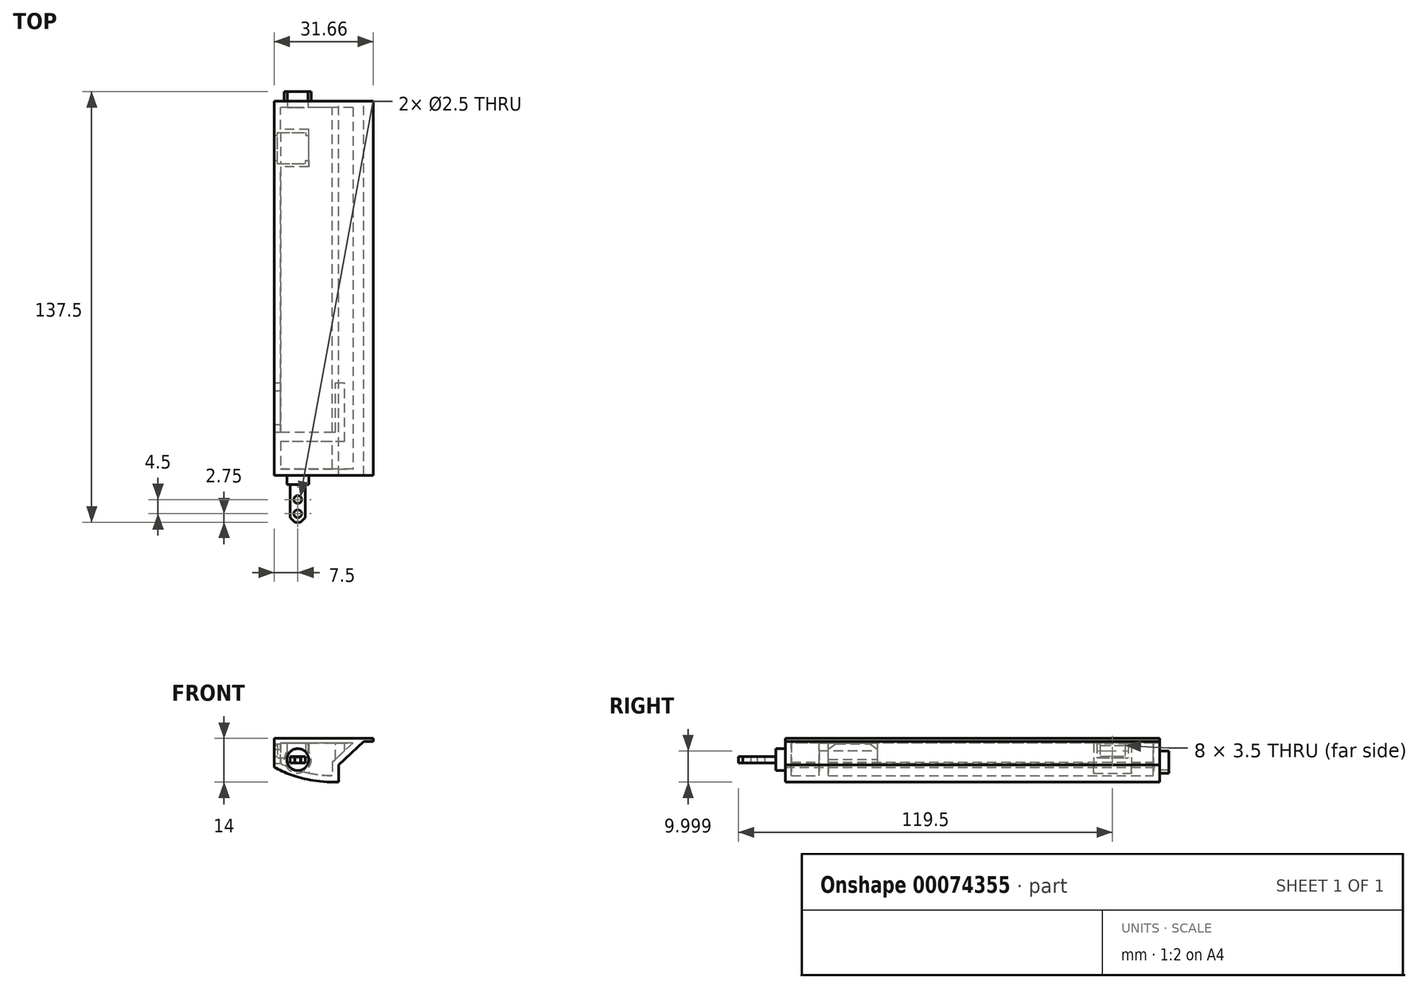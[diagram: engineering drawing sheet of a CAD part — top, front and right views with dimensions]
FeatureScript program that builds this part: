
annotation { "Feature Type Name" : "Feature", "Feature Type Description" : "" }
export const myFeature = defineFeature(function(context is Context, id is Id, definition is map)
    precondition{}
    {
        {
            var Q0;
            Q0=qCreatedBy(makeId("Front.planeOp"),FACE);
            var sketch = newSketch(context, id + "F0", { "sketchPlane" : qUnion([Q0])});
            skCircle(sketch, "E0", {"center": v(7.5, 7.2) * mm, "radius": 4.3 * mm, "construction": true});
            skLineSegment(sketch, "E1", {"start": v(0, 14) * mm, "end": v(31.66, 14) * mm});
            skLineSegment(sketch, "E2", {"start": v(31.66, 13) * mm, "end": v(28.56, 13) * mm});
            skLineSegment(sketch, "E3", {"start": v(28.56, 13) * mm, "end": v(20.5, 5.5) * mm});
            skLineSegment(sketch, "E4", {"start": v(20.5, 5.5) * mm, "end": v(20.5, 0) * mm});
            skFitSpline(sketch, "E5", {"points": [v(20.5, 0) * mm, v(0, 4.8) * mm], "startDerivative": vector(-29.77, 0) * mm, "endDerivative": vector(-14.06, 7.78) * mm});
            skLineSegment(sketch, "E6", {"start": v(0, 10.8) * mm, "end": v(0, 4.8) * mm});
            skLineSegment(sketch, "E7", {"start": v(31.66, 13) * mm, "end": v(31.66, 14) * mm});
            skLineSegment(sketch, "E8", {"start": v(0, 10.8) * mm, "end": v(0, 14) * mm});
            skSolve(sketch);
        }
        {
            var Q0;
            Q0=makeQuery(id+"F0.imprint","IMPRINT",FACE,{"disambiguationData":[TD([[makeQuery(id+"F0.imprint","IMPRINT",EDGE,{"derivedFrom":sQuery(id+"F0.wireOp",EDGE,"E1")}),-1.0]])]});
            extrude(context, id + "F1", {"entities" : qUnion([Q0]), "depth" : 119.5 * mm});
        }
        {
            var Q0;
            Q0=makeQuery(id+"F1.opExtrude","SWEPT_FACE",FACE,{"disambiguationData":[OSD([sQuery(id+"F0.wireOp",EDGE,"E1")])]});
            var Q1;
            Q1=makeQuery(id+"F1.opExtrude","SWEPT_BODY",BODY,{"disambiguationData":[OSD([sQuery(id+"F0.wireOp",EDGE,"E1"),sQuery(id+"F0.wireOp",EDGE,"E2"),sQuery(id+"F0.wireOp",EDGE,"E3"),sQuery(id+"F0.wireOp",EDGE,"E4"),sQuery(id+"F0.wireOp",EDGE,"E5"),sQuery(id+"F0.wireOp",EDGE,"ef3ae709-1856-4767-82a3-158976314dcd"),sQuery(id+"F0.wireOp",EDGE,"E6"),sQuery(id+"F0.wireOp",EDGE,"E7")])]});
            shell(context, id + "F2", {"entities" : qUnion([Q0]), "parts" : qUnion([Q1]), "thickness" : 2 * mm});
        }
        {
            var Q0;
            {var subQ0=sQuery(id+"F0.wireOp",EDGE,"E8");var subQ1=sQuery(id+"F0.wireOp",EDGE,"E7");var subQ2=sQuery(id+"F0.wireOp",EDGE,"E6");var subQ3=sQuery(id+"F0.wireOp",EDGE,"E5");var subQ4=sQuery(id+"F0.wireOp",EDGE,"E4");var subQ5=sQuery(id+"F0.wireOp",EDGE,"E3");var subQ6=sQuery(id+"F0.wireOp",EDGE,"E2");var subQ7=sQuery(id+"F0.wireOp",EDGE,"E1");Q0=makeQuery(id+"F2.opShell","OFFSET_FACE",FACE,{"disambiguationData":[OSD([subQ7,subQ6,subQ5,subQ4,subQ3,subQ2,subQ1,subQ0]),TDD([makeQuery(id+"F1.opExtrude","CAP_FACE",FACE,{"disambiguationData":[OSD([subQ7,subQ6,subQ5,subQ4,subQ3,subQ2,subQ1,subQ0])],"isStart":false})])]});}
            var Q1;
            {var subQ0=sQuery(id+"F0.wireOp",EDGE,"E8");var subQ1=sQuery(id+"F0.wireOp",EDGE,"E7");var subQ2=sQuery(id+"F0.wireOp",EDGE,"E6");var subQ3=sQuery(id+"F0.wireOp",EDGE,"E5");var subQ4=sQuery(id+"F0.wireOp",EDGE,"E4");var subQ5=sQuery(id+"F0.wireOp",EDGE,"E3");var subQ6=sQuery(id+"F0.wireOp",EDGE,"E2");var subQ7=sQuery(id+"F0.wireOp",EDGE,"E1");Q1=makeQuery(id+"F2.opShell","OFFSET_FACE",FACE,{"disambiguationData":[OSD([subQ7,subQ6,subQ5,subQ4,subQ3,subQ2,subQ1,subQ0]),TDD([makeQuery(id+"F1.opExtrude","CAP_FACE",FACE,{"disambiguationData":[OSD([subQ7,subQ6,subQ5,subQ4,subQ3,subQ2,subQ1,subQ0])],"isStart":true})])]});}
            extrude(context, id + "F3", {"entities" : qUnion([Q0]), "endBound" : BoundingType.UP_TO_SURFACE, "endBoundEntityFace" : qUnion([Q1]), "depth" : 25 * mm});
        }
        {
            var Q0;
            Q0=makeQuery(id+"F3.opExtrude","SWEPT_FACE",FACE,{"disambiguationData":[OSD([sQuery(id+"F0.wireOp",EDGE,"E5")])]});
            var Q1;
            Q1=makeQuery(id+"F3.opExtrude","SWEPT_FACE",FACE,{"disambiguationData":[OSD([sQuery(id+"F0.wireOp",EDGE,"E3")])]});
            var Q2;
            Q2=makeQuery(id+"F3.opExtrude","SWEPT_FACE",FACE,{"disambiguationData":[OSD([sQuery(id+"F0.wireOp",EDGE,"E4")])]});
            var Q3;
            Q3=makeQuery(id+"F3.opExtrude","SWEPT_FACE",FACE,{"disambiguationData":[OSD([sQuery(id+"F0.wireOp",EDGE,"E6"),sQuery(id+"F0.wireOp",EDGE,"E8")])]});
            var Q4;
            Q4=makeQuery(id+"F3.opExtrude","CAP_FACE",FACE,{"disambiguationData":[OSD([sQuery(id+"F0.wireOp",EDGE,"E1"),sQuery(id+"F0.wireOp",EDGE,"E2"),sQuery(id+"F0.wireOp",EDGE,"E3"),sQuery(id+"F0.wireOp",EDGE,"E4"),sQuery(id+"F0.wireOp",EDGE,"E5"),sQuery(id+"F0.wireOp",EDGE,"E6"),sQuery(id+"F0.wireOp",EDGE,"E7"),sQuery(id+"F0.wireOp",EDGE,"E8")])],"isStart":true});
            var Q5;
            Q5=makeQuery(id+"F3.opExtrude","CAP_FACE",FACE,{"disambiguationData":[OSD([sQuery(id+"F0.wireOp",EDGE,"E1"),sQuery(id+"F0.wireOp",EDGE,"E2"),sQuery(id+"F0.wireOp",EDGE,"E3"),sQuery(id+"F0.wireOp",EDGE,"E4"),sQuery(id+"F0.wireOp",EDGE,"E5"),sQuery(id+"F0.wireOp",EDGE,"E6"),sQuery(id+"F0.wireOp",EDGE,"E7"),sQuery(id+"F0.wireOp",EDGE,"E8")])],"isStart":false});
            shell(context, id + "F4", {"entities" : qUnion([Q0, Q1, Q2, Q3, Q4, Q5]), "thickness" : 1.5 * mm});
        }
        {
            var Q0;
            Q0=qCreatedBy(makeId("Front.planeOp"),FACE);
            var sketch = newSketch(context, id + "F5", { "sketchPlane" : qUnion([Q0])});
            skCircle(sketch, "E9.0", {"center": v(7.5, 7.2) * mm, "radius": 4.3 * mm});
            skCircle(sketch, "E10", {"center": v(7.5, 7.2) * mm, "radius": 3.3 * mm});
            skSolve(sketch);
        }
        {
            var Q0;
            Q0 = qSketchRegion(id + "F5", true);
            extrude(context, id + "F6", {"entities" : qUnion([Q0]), "operationType" : NewBodyOperationType.ADD, "oppositeDirection" : true, "depth" : 3 * mm});
        }
        {
            var Q0;
            Q0=makeQuery(id+"F5.imprint","IMPRINT",FACE,{"disambiguationData":[TD([[makeQuery(id+"F5.imprint","IMPRINT",EDGE,{"derivedFrom":sQuery(id+"F5.wireOp",EDGE,"E10")}),1.0]])]});
            var Q1;
            Q1=sQuery(id+"F5.wireOp",EDGE,"E10");
            var Q2;
            {var subQ0=sQuery(id+"F0.wireOp",EDGE,"E8");var subQ1=sQuery(id+"F0.wireOp",EDGE,"E7");var subQ2=sQuery(id+"F0.wireOp",EDGE,"E6");var subQ3=sQuery(id+"F0.wireOp",EDGE,"E5");var subQ4=sQuery(id+"F0.wireOp",EDGE,"E4");var subQ5=sQuery(id+"F0.wireOp",EDGE,"E3");var subQ6=sQuery(id+"F0.wireOp",EDGE,"E2");var subQ7=sQuery(id+"F0.wireOp",EDGE,"E1");Q2=makeQuery(id+"F2.opShell","OFFSET_FACE",FACE,{"disambiguationData":[OSD([subQ7,subQ6,subQ5,subQ4,subQ3,subQ2,subQ1,subQ0]),TDD([makeQuery(id+"F1.opExtrude","CAP_FACE",FACE,{"disambiguationData":[OSD([subQ7,subQ6,subQ5,subQ4,subQ3,subQ2,subQ1,subQ0])],"isStart":true})])]});}
            extrude(context, id + "F7", {"entities" : qUnion([Q0]), "operationType" : NewBodyOperationType.REMOVE, "surfaceEntities" : qUnion([Q1]), "endBound" : BoundingType.UP_TO_SURFACE, "endBoundEntityFace" : qUnion([Q2]), "depth" : 25 * mm});
        }
        {
            var Q0;
            Q0=makeQuery(id+"F1.opExtrude","CAP_FACE",FACE,{"disambiguationData":[OSD([sQuery(id+"F0.wireOp",EDGE,"E1"),sQuery(id+"F0.wireOp",EDGE,"E2"),sQuery(id+"F0.wireOp",EDGE,"E3"),sQuery(id+"F0.wireOp",EDGE,"E4"),sQuery(id+"F0.wireOp",EDGE,"E5"),sQuery(id+"F0.wireOp",EDGE,"ef3ae709-1856-4767-82a3-158976314dcd"),sQuery(id+"F0.wireOp",EDGE,"E6"),sQuery(id+"F0.wireOp",EDGE,"E7")])],"isStart":false});
            var sketch = newSketch(context, id + "F8", { "sketchPlane" : qUnion([Q0])});
            skPoint(sketch, "E11.0", {"position": v(7.5, 7.2) * mm});
            skCircle(sketch, "E12", {"center": v(7.5, 7.2) * mm, "radius": 3.5 * mm});
            skSolve(sketch);
        }
        {
            var Q0;
            Q0=makeQuery(id+"F8.imprint","IMPRINT",FACE,{"disambiguationData":[TD([[makeQuery(id+"F8.imprint","IMPRINT",EDGE,{"derivedFrom":sQuery(id+"F8.wireOp",EDGE,"E12")}),1.0]])]});
            extrude(context, id + "F9", {"entities" : qUnion([Q0]), "operationType" : NewBodyOperationType.ADD, "depth" : 3 * mm});
        }
        {
            var Q0;
            Q0=makeQuery(id+"F1.opExtrude","SWEPT_FACE",FACE,{"disambiguationData":[OSD([sQuery(id+"F0.wireOp",EDGE,"E1")])]});
            var sketch = newSketch(context, id + "F10", { "sketchPlane" : qUnion([Q0])});
            skLineSegment(sketch, "E13", {"start": v(4.2, -2) * mm, "end": v(4.2, 3) * mm});
            skLineSegment(sketch, "E14", {"start": v(10.8, 3) * mm, "end": v(10.8, -2) * mm});
            skLineSegment(sketch, "E15", {"start": v(10.8, -2) * mm, "end": v(4.2, -2) * mm});
            skLineSegment(sketch, "E16", {"start": v(10.8, 3) * mm, "end": v(4.2, 3) * mm});
            skSolve(sketch);
        }
        {
            var Q0;
            Q0 = qSketchRegion(id + "F10", true);
            var Q1;
            {var subQ0=sQuery(id+"F5.wireOp",EDGE,"E10");Q1=makeQuery(id+"F7.boolean.opBoolean","MERGE",FACE,{"derivedFrom":[makeQuery(id+"F6.opExtrude","SWEPT_FACE",FACE,{"disambiguationData":[OSD([subQ0])]}),makeQuery(id+"F7.opExtrude","SWEPT_FACE",FACE,{"disambiguationData":[OSD([subQ0])]})]});}
            extrude(context, id + "F11", {"entities" : qUnion([Q0]), "operationType" : NewBodyOperationType.REMOVE, "endBound" : BoundingType.UP_TO_SURFACE, "oppositeDirection" : true, "endBoundEntityFace" : qUnion([Q1]), "depth" : 25 * mm});
        }
        {
            var Q0;
            Q0=makeQuery(id+"F3.opExtrude","CAP_FACE",FACE,{"disambiguationData":[OSD([sQuery(id+"F0.wireOp",EDGE,"E1"),sQuery(id+"F0.wireOp",EDGE,"E2"),sQuery(id+"F0.wireOp",EDGE,"E3"),sQuery(id+"F0.wireOp",EDGE,"E4"),sQuery(id+"F0.wireOp",EDGE,"E5"),sQuery(id+"F0.wireOp",EDGE,"E6"),sQuery(id+"F0.wireOp",EDGE,"E7"),sQuery(id+"F0.wireOp",EDGE,"E8")])],"isStart":false});
            var sketch = newSketch(context, id + "F12", { "sketchPlane" : qUnion([Q0])});
            skLineSegment(sketch, "E17.0", {"start": v(-10.8, 7.2) * mm, "end": v(-10.8, 14) * mm});
            skLineSegment(sketch, "E18.0", {"start": v(-4.2, 7.2) * mm, "end": v(-4.2, 14) * mm});
            skSolve(sketch);
        }
        {
            var Q0;
            {var subQ0=sQuery(id+"F12.wireOp",EDGE,"E17.0");var subQ1=sQuery(id+"F0.wireOp",EDGE,"E1");var subQ2=makeQuery(id+"F3.opExtrude","CAP_EDGE",EDGE,{"disambiguationData":[OSD([subQ1])],"isStart":false});var subQ3=makeQuery(id+"F12.imprint","INTERSECT",VERTEX,{"derivedFrom":[subQ2,subQ0]});Q0=makeQuery(id+"F12.imprint","IMPRINT",FACE,{"disambiguationData":[TD([[makeQuery(id+"F12.imprint","IMPRINT",EDGE,{"disambiguationData":[TD([[subQ3,-1.0]])],"derivedFrom":subQ2}),-1.0]])]});}
            var Q1;
            {var subQ0=sQuery(id+"F0.wireOp",EDGE,"E4");var subQ1=sQuery(id+"F0.wireOp",EDGE,"E3");var subQ2=sQuery(id+"F0.wireOp",EDGE,"E2");var subQ3=sQuery(id+"F0.wireOp",EDGE,"E1");var subQ4=sQuery(id+"F0.wireOp",EDGE,"E5");var subQ5=sQuery(id+"F0.wireOp",EDGE,"E8");var subQ6=sQuery(id+"F0.wireOp",EDGE,"E6");var subQ7=sQuery(id+"F0.wireOp",EDGE,"E7");Q1=makeQuery(id+"F6.boolean.opBoolean","SPLIT",FACE,{"disambiguationData":[TD([makeQuery(id+"F1.opExtrude","SWEPT_FACE",FACE,{"disambiguationData":[OSD([subQ3])]})])],"derivedFrom":makeQuery(id+"F1.opExtrude","CAP_FACE",FACE,{"disambiguationData":[OSD([subQ3,subQ2,subQ1,subQ0,subQ4,subQ6,subQ7,subQ5])],"isStart":true})});}
            extrude(context, id + "F13", {"entities" : qUnion([Q0]), "operationType" : NewBodyOperationType.ADD, "endBound" : BoundingType.UP_TO_SURFACE, "endBoundEntityFace" : qUnion([Q1]), "depth" : 25 * mm});
        }
        {
            var Q0;
            Q0=makeQuery(id+"F2.opShell","OFFSET_FACE",FACE,{"disambiguationData":[OSD([sQuery(id+"F0.wireOp",EDGE,"E6")])]});
            var sketch = newSketch(context, id + "F14", { "sketchPlane" : qUnion([Q0])});
            skLineSegment(sketch, "E19.rect.bottom", {"start": v(-20, 12.25) * mm, "end": v(-10, 12.25) * mm});
            skLineSegment(sketch, "E19.rect.top", {"start": v(-20, 7.75) * mm, "end": v(-10, 7.75) * mm});
            skLineSegment(sketch, "E19.rect.left", {"start": v(-20, 12.25) * mm, "end": v(-20, 7.75) * mm});
            skLineSegment(sketch, "E19.rect.right", {"start": v(-10, 12.25) * mm, "end": v(-10, 7.75) * mm});
            skPoint(sketch, "E19.rect.middle", {"position": v(-15, 10) * mm});
            skLineSegment(sketch, "E20.rect.bottom", {"start": v(-19, 11.75) * mm, "end": v(-11, 11.75) * mm});
            skLineSegment(sketch, "E20.rect.top", {"start": v(-19, 8.25) * mm, "end": v(-11, 8.25) * mm});
            skLineSegment(sketch, "E20.rect.left", {"start": v(-19, 11.75) * mm, "end": v(-19, 8.25) * mm});
            skLineSegment(sketch, "E20.rect.right", {"start": v(-11, 11.75) * mm, "end": v(-11, 8.25) * mm});
            skLineSegment(sketch, "E21", {"start": v(-90, 6) * mm, "end": v(-90, 10.5) * mm});
            skLineSegment(sketch, "E22", {"start": v(-90, 6) * mm, "end": v(-97.85, 6) * mm});
            skLineSegment(sketch, "E23", {"start": v(-97.85, 6) * mm, "end": v(-97.85, 12.2) * mm, "construction": true});
            skLineSegment(sketch, "E24", {"start": v(-97.85, 12.2) * mm, "end": v(-92.45, 12.2) * mm});
            skLineSegment(sketch, "E25", {"start": v(-92.45, 12.2) * mm, "end": v(-90, 10.5) * mm});
            skLineSegment(sketch, "E26.MirrorCS", {"start": v(-105.7, 6) * mm, "end": v(-97.85, 6) * mm});
            skLineSegment(sketch, "E27.MirrorCS", {"start": v(-105.7, 6) * mm, "end": v(-105.7, 10.5) * mm});
            skLineSegment(sketch, "E28.MirrorCS", {"start": v(-103.25, 12.2) * mm, "end": v(-105.7, 10.5) * mm});
            skLineSegment(sketch, "E29.MirrorCS", {"start": v(-97.85, 12.2) * mm, "end": v(-103.25, 12.2) * mm});
            skPoint(sketch, "E30", {"position": v(-2, 10) * mm});
            skSolve(sketch);
        }
        {
            var Q0;
            Q0=makeQuery(id+"F14.imprint","IMPRINT",FACE,{"disambiguationData":[TD([[makeQuery(id+"F14.imprint","IMPRINT",EDGE,{"derivedFrom":sQuery(id+"F14.wireOp",EDGE,"E20.rect.bottom")}),-1.0]])]});
            var Q1;
            Q1=makeQuery(id+"F1.opExtrude","SWEPT_FACE",FACE,{"disambiguationData":[OSD([sQuery(id+"F0.wireOp",EDGE,"E6")])]});
            extrude(context, id + "F15", {"entities" : qUnion([Q0]), "operationType" : NewBodyOperationType.REMOVE, "endBound" : BoundingType.UP_TO_SURFACE, "oppositeDirection" : true, "endBoundEntityFace" : qUnion([Q1]), "depth" : 25 * mm});
        }
        {
            var Q0;
            Q0=makeQuery(id+"F14.imprint","IMPRINT",FACE,{"disambiguationData":[TD([[makeQuery(id+"F14.imprint","IMPRINT",EDGE,{"derivedFrom":sQuery(id+"F14.wireOp",EDGE,"E19.rect.bottom")}),-1.0]])]});
            var Q1;
            Q1=makeQuery(id+"F2.opShell","OFFSET_FACE",FACE,{"disambiguationData":[OSD([sQuery(id+"F0.wireOp",EDGE,"ef3ae709-1856-4767-82a3-158976314dcd")])]});
            extrude(context, id + "F16", {"entities" : qUnion([Q0]), "operationType" : NewBodyOperationType.REMOVE, "oppositeDirection" : true, "endBoundEntityFace" : qUnion([Q1]), "depth" : 1 * mm, "hasSecondDirection" : true, "secondDirectionOppositeDirection" : false, "secondDirectionDepth" : 1 * mm});
        }
        {
            var Q0;
            Q0=makeQuery(id+"F14.imprint","IMPRINT",FACE,{"disambiguationData":[TD([[makeQuery(id+"F14.imprint","IMPRINT",EDGE,{"derivedFrom":sQuery(id+"F14.wireOp",EDGE,"E21")}),1.0]])]});
            var Q1;
            Q1=makeQuery(id+"F1.opExtrude","SWEPT_FACE",FACE,{"disambiguationData":[OSD([sQuery(id+"F0.wireOp",EDGE,"E6")])]});
            var Q2;
            Q2=makeQuery(id+"F2.opShell","OFFSET_FACE",FACE,{"disambiguationData":[OSD([sQuery(id+"F0.wireOp",EDGE,"E8")])]});
            extrude(context, id + "F17", {"entities" : qUnion([Q0]), "operationType" : NewBodyOperationType.REMOVE, "endBound" : BoundingType.UP_TO_SURFACE, "oppositeDirection" : true, "endBoundEntityFace" : qUnion([Q1]), "depth" : 25 * mm});
        }
        {
            var Q0;
            {var subQ0=sQuery(id+"F0.wireOp",EDGE,"E1");var subQ1=makeQuery(id+"F4.opShell","OFFSET_EDGE",EDGE,{"disambiguationData":[OSD([subQ0]),TDD([makeQuery(id+"F3.opExtrude","CAP_EDGE",EDGE,{"disambiguationData":[OSD([subQ0])],"isStart":false})])]});Q0=makeQuery(id+"F13.boolean.opBoolean","MERGE",FACE,{"derivedFrom":[makeQuery(id+"F4.opShell","OFFSET_FACE",FACE,{"disambiguationData":[OSD([subQ0])]}),makeQuery(id+"F13.opExtrude","SWEPT_FACE",FACE,{"disambiguationData":[OSD([subQ0]),TDD([makeQuery(id+"F12.imprint","IMPRINT",EDGE,{"disambiguationData":[TD([[makeQuery(id+"F12.imprint","INTERSECT",VERTEX,{"derivedFrom":[subQ1,sQuery(id+"F12.wireOp",EDGE,"E17.0")]}),-1.0]])],"derivedFrom":subQ1})])]})]});}
            var sketch = newSketch(context, id + "F18", { "sketchPlane" : qUnion([Q0])});
            skLineSegment(sketch, "E31.rect.top", {"start": v(19.5, 90) * mm, "end": v(22.5, 90) * mm});
            skLineSegment(sketch, "E31.rect.right", {"start": v(22.5, 108.7) * mm, "end": v(22.5, 90) * mm});
            skLineSegment(sketch, "E32", {"start": v(22.5, 108.7) * mm, "end": v(2, 108.7) * mm});
            skLineSegment(sketch, "E33", {"start": v(2, 108.7) * mm, "end": v(2, 105.7) * mm});
            skLineSegment(sketch, "E34", {"start": v(2, 105.7) * mm, "end": v(19.5, 105.7) * mm});
            skLineSegment(sketch, "E35", {"start": v(19.5, 105.7) * mm, "end": v(19.5, 90) * mm});
            skPoint(sketch, "E36.0", {"position": v(2, 90) * mm});
            skPoint(sketch, "E37.0", {"position": v(2, 105.7) * mm});
            skSolve(sketch);
        }
        {
            var Q0;
            Q0 = qSketchRegion(id + "F18", true);
            var Q1;
            Q1=makeQuery(id+"F1.opExtrude","SWEPT_BODY",BODY,{"disambiguationData":[OSD([sQuery(id+"F0.wireOp",EDGE,"E1"),sQuery(id+"F0.wireOp",EDGE,"E2"),sQuery(id+"F0.wireOp",EDGE,"E3"),sQuery(id+"F0.wireOp",EDGE,"E4"),sQuery(id+"F0.wireOp",EDGE,"E5"),sQuery(id+"F0.wireOp",EDGE,"E6"),sQuery(id+"F0.wireOp",EDGE,"E7"),sQuery(id+"F0.wireOp",EDGE,"E8")])]});
            extrude(context, id + "F19", {"entities" : qUnion([Q0]), "operationType" : NewBodyOperationType.ADD, "endBound" : BoundingType.UP_TO_BODY, "endBoundEntityBody" : qUnion([Q1]), "depth" : 25 * mm});
        }
        {
            var Q0;
            Q0=makeQuery(id+"F9.opExtrude","CAP_FACE",FACE,{"disambiguationData":[OSD([sQuery(id+"F8.wireOp",EDGE,"E12")])],"isStart":false});
            var sketch = newSketch(context, id + "F20", { "sketchPlane" : qUnion([Q0])});
            skLineSegment(sketch, "E38.rect.bottom", {"start": v(9.9, 8.2) * mm, "end": v(5.1, 8.2) * mm});
            skLineSegment(sketch, "E38.rect.top", {"start": v(9.9, 6.2) * mm, "end": v(5.1, 6.2) * mm});
            skLineSegment(sketch, "E38.rect.left", {"start": v(9.9, 8.2) * mm, "end": v(9.9, 6.2) * mm});
            skLineSegment(sketch, "E38.rect.right", {"start": v(5.1, 8.2) * mm, "end": v(5.1, 6.2) * mm});
            skPoint(sketch, "E38.rect.middle", {"position": v(7.5, 7.2) * mm});
            skSolve(sketch);
        }
        {
            var Q0;
            Q0=makeQuery(id+"F20.imprint","IMPRINT",FACE,{"disambiguationData":[TD([[makeQuery(id+"F20.imprint","IMPRINT",EDGE,{"derivedFrom":sQuery(id+"F20.wireOp",EDGE,"E38.rect.bottom")}),1.0]])]});
            extrude(context, id + "F21", {"entities" : qUnion([Q0]), "operationType" : NewBodyOperationType.ADD, "depth" : 12 * mm});
        }
        {
            var Q0;
            Q0=makeQuery(id+"F21.opExtrude","CAP_EDGE",EDGE,{"disambiguationData":[OSD([sQuery(id+"F20.wireOp",EDGE,"E38.rect.right")])],"isStart":false});
            var Q1;
            Q1=makeQuery(id+"F21.opExtrude","CAP_EDGE",EDGE,{"disambiguationData":[OSD([sQuery(id+"F20.wireOp",EDGE,"E38.rect.left")])],"isStart":false});
            chamfer(context, id + "F22", {"entities" : qUnion([Q0, Q1]), "width" : 1.5 * mm});
        }
        {
            var Q0;
            Q0=makeQuery(id+"F21.opExtrude","SWEPT_FACE",FACE,{"disambiguationData":[OSD([sQuery(id+"F20.wireOp",EDGE,"E38.rect.top")])]});
            var sketch = newSketch(context, id + "F23", { "sketchPlane" : qUnion([Q0])});
            skPoint(sketch, "E39", {"position": v(7.5, 122.5) * mm});
            skPoint(sketch, "E40", {"position": v(7.5, 127.25) * mm});
            skPoint(sketch, "E41", {"position": v(7.5, 131.75) * mm});
            skSolve(sketch);
        }
        {
            var Q0;
            Q0=sQuery(id+"F23.wireOp",VERTEX,"E40");
            var Q1;
            Q1=sQuery(id+"F23.wireOp",VERTEX,"E41");
            var Q2;
            Q2=makeQuery(id+"F1.opExtrude","SWEPT_BODY",BODY,{"disambiguationData":[OSD([sQuery(id+"F0.wireOp",EDGE,"E1"),sQuery(id+"F0.wireOp",EDGE,"E2"),sQuery(id+"F0.wireOp",EDGE,"E3"),sQuery(id+"F0.wireOp",EDGE,"E4"),sQuery(id+"F0.wireOp",EDGE,"E5"),sQuery(id+"F0.wireOp",EDGE,"E6"),sQuery(id+"F0.wireOp",EDGE,"E7"),sQuery(id+"F0.wireOp",EDGE,"E8")])]});
            hole(context, id + "F24", {"style" : HoleStyle.SIMPLE, "holeDiameter" : 2.5 * mm, "endStyle" : HoleEndStyle.THROUGH, "locations" : qUnion([Q0, Q1]), "scope" : qUnion([Q2])});
        }
        {
            var Q0;
            Q0=makeQuery(id+"F16.boolean.opBoolean","COPY",FACE,{"derivedFrom":makeQuery(id+"F16.opExtrude","SWEPT_FACE",FACE,{"disambiguationData":[OSD([sQuery(id+"F14.wireOp",EDGE,"E19.rect.top")])]})});
            var sketch = newSketch(context, id + "F25", { "sketchPlane" : qUnion([Q0])});
            skPoint(sketch, "E42.0", {"position": v(2, -15) * mm});
            skLineSegment(sketch, "E43", {"start": v(2, -15) * mm, "end": v(17.78, -15) * mm, "construction": true});
            skLineSegment(sketch, "E44", {"start": v(2, -21) * mm, "end": v(11, -21) * mm});
            skLineSegment(sketch, "E45", {"start": v(11, -21) * mm, "end": v(11, -19) * mm});
            skLineSegment(sketch, "E46", {"start": v(11, -19) * mm, "end": v(10, -19) * mm});
            skLineSegment(sketch, "E47", {"start": v(10, -19) * mm, "end": v(10, -20) * mm});
            skLineSegment(sketch, "E48", {"start": v(10, -20) * mm, "end": v(2, -20) * mm});
            skLineSegment(sketch, "E49", {"start": v(2, -20) * mm, "end": v(2, -21) * mm});
            skLineSegment(sketch, "E50.0", {"start": v(2, -10) * mm, "end": v(2, -20) * mm, "construction": true});
            skLineSegment(sketch, "E51.MirrorCS", {"start": v(2, -10) * mm, "end": v(2, -9) * mm});
            skLineSegment(sketch, "E52.MirrorCS", {"start": v(2, -9) * mm, "end": v(11, -9) * mm});
            skLineSegment(sketch, "E53.MirrorCS", {"start": v(11, -9) * mm, "end": v(11, -11) * mm});
            skLineSegment(sketch, "E54.MirrorCS", {"start": v(11, -11) * mm, "end": v(10, -11) * mm});
            skLineSegment(sketch, "E55.MirrorCS", {"start": v(10, -11) * mm, "end": v(10, -10) * mm});
            skLineSegment(sketch, "E56.MirrorCS", {"start": v(10, -10) * mm, "end": v(2, -10) * mm});
            skLineSegment(sketch, "E57", {"start": v(11, -19) * mm, "end": v(11, -11) * mm});
            skLineSegment(sketch, "E58", {"start": v(2, -20) * mm, "end": v(2, -10) * mm});
            skSolve(sketch);
        }
        {
            var Q0;
            Q0=makeQuery(id+"F25.imprint","IMPRINT",FACE,{"disambiguationData":[TD([[makeQuery(id+"F25.imprint","IMPRINT",EDGE,{"derivedFrom":sQuery(id+"F25.wireOp",EDGE,"E51.MirrorCS")}),-1.0]])]});
            var Q1;
            Q1=makeQuery(id+"F25.imprint","IMPRINT",FACE,{"disambiguationData":[TD([[makeQuery(id+"F25.imprint","IMPRINT",EDGE,{"derivedFrom":sQuery(id+"F25.wireOp",EDGE,"E44")}),1.0]])]});
            var Q2;
            Q2=makeQuery(id+"F16.boolean.opBoolean","COPY",FACE,{"derivedFrom":makeQuery(id+"F16.opExtrude","SWEPT_FACE",FACE,{"disambiguationData":[OSD([sQuery(id+"F14.wireOp",EDGE,"E19.rect.top")])]})});
            var Q3;
            Q3=makeQuery(id+"F3.opExtrude","SWEPT_BODY",BODY,{"disambiguationData":[OSD([sQuery(id+"F0.wireOp",EDGE,"E1"),sQuery(id+"F0.wireOp",EDGE,"E2"),sQuery(id+"F0.wireOp",EDGE,"E3"),sQuery(id+"F0.wireOp",EDGE,"E4"),sQuery(id+"F0.wireOp",EDGE,"E5"),sQuery(id+"F0.wireOp",EDGE,"E6"),sQuery(id+"F0.wireOp",EDGE,"E7"),sQuery(id+"F0.wireOp",EDGE,"E8")])]});
            var Q4;
            Q4=makeQuery(id+"F1.opExtrude","SWEPT_FACE",FACE,{"disambiguationData":[OSD([sQuery(id+"F0.wireOp",EDGE,"E8")])]});
            extrude(context, id + "F26", {"entities" : qUnion([Q0, Q1]), "operationType" : NewBodyOperationType.ADD, "endBound" : BoundingType.UP_TO_NEXT, "endBoundEntityFace" : qUnion([Q2]), "endBoundEntityBody" : qUnion([Q3]), "depth" : 25 * mm, "hasSecondDirection" : true, "secondDirectionBound" : SecondDirectionBoundingType.UP_TO_NEXT, "secondDirectionOppositeDirection" : true, "secondDirectionBoundEntityFace" : qUnion([Q4]), "secondDirectionDepth" : 25 * mm});
        }
        {
            var Q0;
            Q0=makeQuery(id+"F25.imprint","IMPRINT",FACE,{"disambiguationData":[TD([[makeQuery(id+"F25.imprint","IMPRINT",EDGE,{"derivedFrom":sQuery(id+"F25.wireOp",EDGE,"E46")}),-1.0]])]});
            var Q1;
            Q1=makeQuery(id+"F16.boolean.opBoolean","COPY",FACE,{"derivedFrom":makeQuery(id+"F16.opExtrude","SWEPT_FACE",FACE,{"disambiguationData":[OSD([sQuery(id+"F14.wireOp",EDGE,"E19.rect.bottom")])]})});
            extrude(context, id + "F27", {"entities" : qUnion([Q0]), "operationType" : NewBodyOperationType.ADD, "endBound" : BoundingType.UP_TO_NEXT, "oppositeDirection" : true, "endBoundEntityFace" : qUnion([Q1]), "depth" : 25 * mm});
        }
    });
